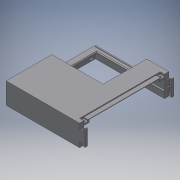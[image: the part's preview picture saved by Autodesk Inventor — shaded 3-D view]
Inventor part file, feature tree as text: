
AUTODESK INVENTOR PART (.ipt)
format: ipt  version: 2016 SP2 (Build 200236200, 236)  size: 877,056 bytes
history: native  units: mm
features: sketch x24, other x5, thread x2, revolve x2
ambient origin geometry x8: Origin, YZ Plane, XZ Plane, XY Plane, X Axis, Y Axis, Z Axis, Center Point
bodies: Volumenkörper2 (feature_tree), Volumenkörper3 (feature_tree), Volumenkörper1 (feature_tree)
feature tree (33):
  other  "Case_side_back.ipt"
  thread  "Gewinde1"  [1 undecoded]
  thread  "Gewinde2"  [1 undecoded]
  revolve  "Umdrehung1"
  other  "Spirale1"
  revolve  "Umdrehung2"
  other  "Spirale2"
  other  "Volumenkörper1::Case_side_back.ipt"
  other  "Bezeichnung1"
  sketch  "Skizze1"  dims[d3=10.0mm d4=0.0mm]
  sketch  "Skizze2"  dims[d5=60.0deg d6=0.240125mm d7=0.240125mm]
  sketch  "Skizze3"  dims[d10=1.5mm]
  sketch  "Skizze4"  dims[d12=60.0deg]
  sketch  "Skizze7"  dims[d14=0.0mm]
  sketch  "Skizze8"  dims[d15=1.5015mm d16=7.0mm d17=10.0mm d18=0.0mm d19=0.0mm d20=0.0mm d21=0.0mm d22=0.0mm]
  sketch  "Skizze9"  dims[d23=60.0deg d24=0.240125mm d25=0.240125mm]
  sketch  "Skizze10"  dims[d28=1.5mm]
  sketch  "Skizze11"  dims[d30=60.0deg]
  sketch  "Skizze12"  dims[d32=0.0mm]
  sketch  "Skizze13"  dims[d33=1.5015mm d34=7.0mm d35=10.0mm d36=0.0mm d37=0.0mm d38=0.0mm d39=0.0mm d40=0.0mm]
  sketch  "Skizze14"
  sketch  "Skizze15"
  sketch  "Skizze16"
  sketch  "Skizze17"
  sketch  "Skizze18"
  sketch  "Skizze19"
  sketch  "Skizze20"
  sketch  "Skizze21"
  sketch  "Skizze22"
  sketch  "Skizze23"
  sketch  "Skizze24"
  sketch  "Skizze25"
  sketch  "Skizze26"
note: 2 required parameter values undecoded (feature->parameter linkage not recoverable at this tier; creation-order binding heuristic only, values carry confidence <= 0.55)
